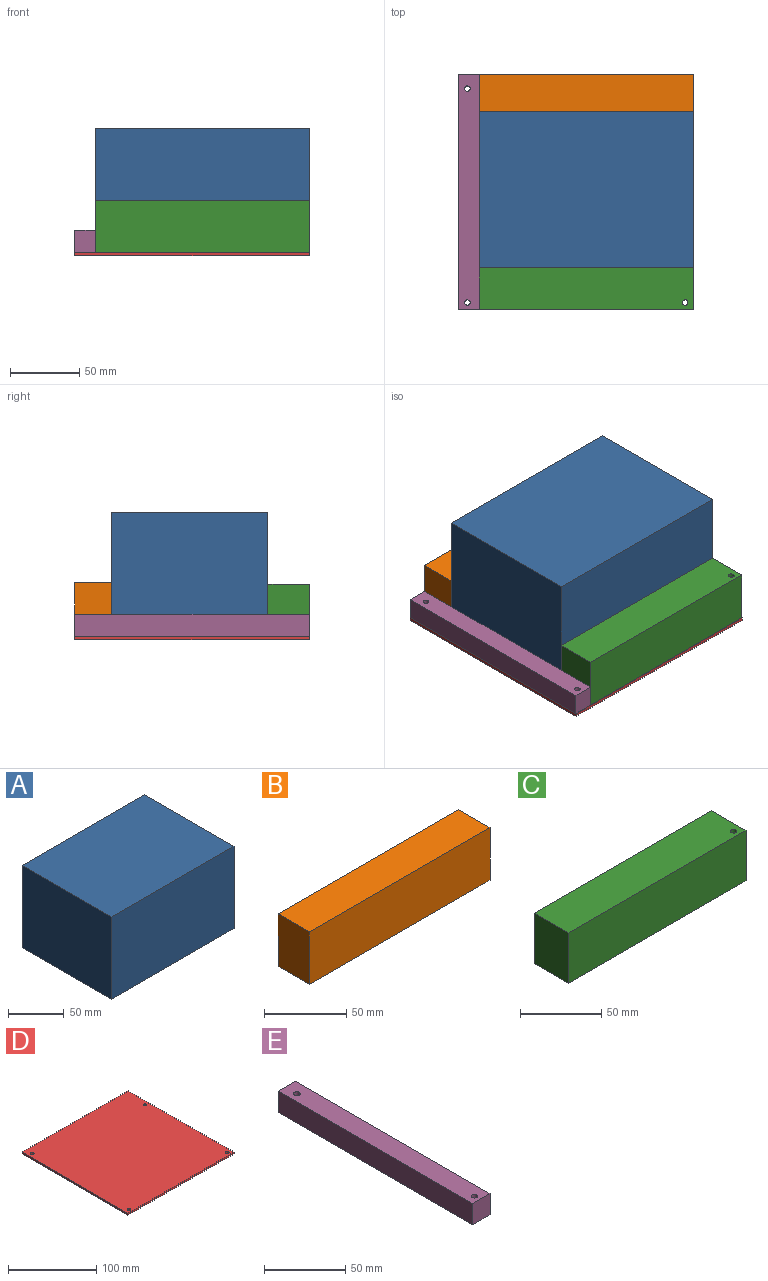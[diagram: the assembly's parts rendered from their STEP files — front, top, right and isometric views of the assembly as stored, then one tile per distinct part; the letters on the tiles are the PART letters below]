
ASSEMBLY  parts=5 mates=12
PART A: 6 faces, bbox 155x113x90 mm
  f0: plane 155x90mm, normal (0,1,0), area 13950mm2, adj f1,f3,f4,f5
  f1: plane 113x90mm, normal (-1,0,0), area 10170mm2, adj f0,f2,f4,f5
  f2: plane 155x90mm, normal (0,-1,0), area 13950mm2, adj f1,f3,f4,f5
  f3: plane 113x90mm, normal (1,0,0), area 10170mm2, adj f0,f2,f4,f5
  f4: plane 155x113mm, normal (0,0,1), area 17515mm2, adj f0,f1,f2,f3
  f5: plane 155x113mm, normal (0,0,-1), area 17515mm2, adj f0,f1,f2,f3
PART B: 6 faces, bbox 155x27x39 mm
  f0: plane 155x39mm, normal (0,1,0), area 6045mm2, adj f1,f3,f4,f5
  f1: plane 39x27mm, normal (-1,0,0), area 1053mm2, adj f0,f2,f4,f5
  f2: plane 155x39mm, normal (0,-1,0), area 6045mm2, adj f1,f3,f4,f5
  f3: plane 39x27mm, normal (1,0,0), area 1053mm2, adj f0,f2,f4,f5
  f4: plane 155x27mm, normal (0,0,1), area 4185mm2, adj f0,f1,f2,f3
  f5: plane 155x27mm, normal (0,0,-1), area 4185mm2, adj f0,f1,f2,f3
PART C: 7 faces, bbox 155x30x38 mm
  f0: plane 38x30mm, normal (-1,0,0), area 1140mm2, adj f1,f3,f5,f6
  f1: plane 155x38mm, normal (0,-1,0), area 5890mm2, adj f0,f2,f5,f6
  f2: plane 38x30mm, normal (1,0,0), area 1140mm2, adj f1,f3,f5,f6
  f3: plane 155x38mm, normal (0,1,0), area 5890mm2, adj f0,f2,f5,f6
  f4: cylinder r=1.98mm len=38mm, axis (0,0,-1), area 472.7mm2, adj f5,f6
  f5: plane 155x30mm, normal (0,0,1), area 4637.7mm2, adj f0,f1,f2,f3,f4
  f6: plane 155x30mm, normal (0,0,-1), area 4637.7mm2, adj f0,f1,f2,f3,f4
PART D: 10 faces, bbox 170x170x2.4 mm
  f0: plane 170x2.36mm, normal (-1,0,0), area 401.2mm2, adj f1,f6,f8,f9
  f1: plane 170x2.36mm, normal (0,-1,0), area 401.2mm2, adj f0,f2,f8,f9
  f2: plane 170x2.36mm, normal (1,0,0), area 401.2mm2, adj f1,f6,f8,f9
  f3: cylinder r=1.98mm len=3.96mm, axis (0,0,-1), area 29.4mm2, adj f8,f9
  f4: cylinder r=1.98mm len=3.96mm, axis (0,0,-1), area 29.4mm2, adj f8,f9
  f5: cylinder r=1.98mm len=3.96mm, axis (0,0,-1), area 29.4mm2, adj f8,f9
  f6: plane 170x2.36mm, normal (0,1,0), area 401.2mm2, adj f0,f2,f8,f9
  f7: cylinder r=1.98mm len=3.96mm, axis (0,0,-1), area 29.4mm2, adj f8,f9
  f8: plane 170x170mm, normal (0,0,1), area 28850.7mm2, adj f0,f1,f2,f3,f4,f5,f6,f7
  f9: plane 170x170mm, normal (0,0,-1), area 28850.7mm2, adj f0,f1,f2,f3,f4,f5,f6,f7
PART E: 8 faces, bbox 15x170x16 mm
  f0: plane 170x16mm, normal (1,0,0), area 2720mm2, adj f1,f4,f6,f7
  f1: plane 16x15mm, normal (0,1,0), area 240mm2, adj f0,f2,f6,f7
  f2: plane 170x16mm, normal (-1,0,0), area 2720mm2, adj f1,f4,f6,f7
  f3: cylinder r=1.98mm len=16mm, axis (0,0,-1), area 199.1mm2, adj f6,f7
  f4: plane 16x15mm, normal (0,-1,0), area 240mm2, adj f0,f2,f6,f7
  f5: cylinder r=1.98mm len=16mm, axis (0,0,-1), area 199.1mm2, adj f6,f7
  f6: plane 170x15mm, normal (0,0,1), area 2525.4mm2, adj f0,f1,f2,f3,f4,f5
  f7: plane 170x15mm, normal (0,0,-1), area 2525.4mm2, adj f0,f1,f2,f3,f4,f5
PLACE A at identity
PLACE B at identity
PLACE C at identity
PLACE D at identity
PLACE E at identity
MATE planar B.f5 <-> D.f8  axis (0,0,-1) through (92.5,156.5,2.36)mm
MATE planar C.f0 <-> E.f0  axis (-1,0,0) through (15,15,40.36)mm
MATE planar A.f5 <-> D.f8  axis (0,0,-1) through (92.5,86.5,2.36)mm
MATE planar E.f0 <-> A.f1  axis (1,0,0) through (15,85,10.36)mm
MATE planar D.f8 <-> C.f6  axis (0,0,1) through (85,85.01,2.36)mm
MATE planar E.f2 <-> D.f0  axis (-1,0,0) through (0,85,10.36)mm
MATE planar D.f6 <-> E.f1  axis (0,1,0) through (85,170,1.18)mm
MATE planar E.f7 <-> D.f8  axis (0,0,-1) through (7.51,85.03,2.36)mm
MATE planar A.f0 <-> B.f2  axis (0,1,0) through (92.5,143,47.36)mm
MATE planar B.f0 <-> D.f6  axis (0,1,0) through (92.5,170,21.86)mm
MATE planar A.f2 <-> C.f3  axis (0,-1,0) through (92.5,30,47.36)mm
MATE planar B.f3 <-> D.f2  axis (1,0,0) through (170,156.5,21.86)mm
